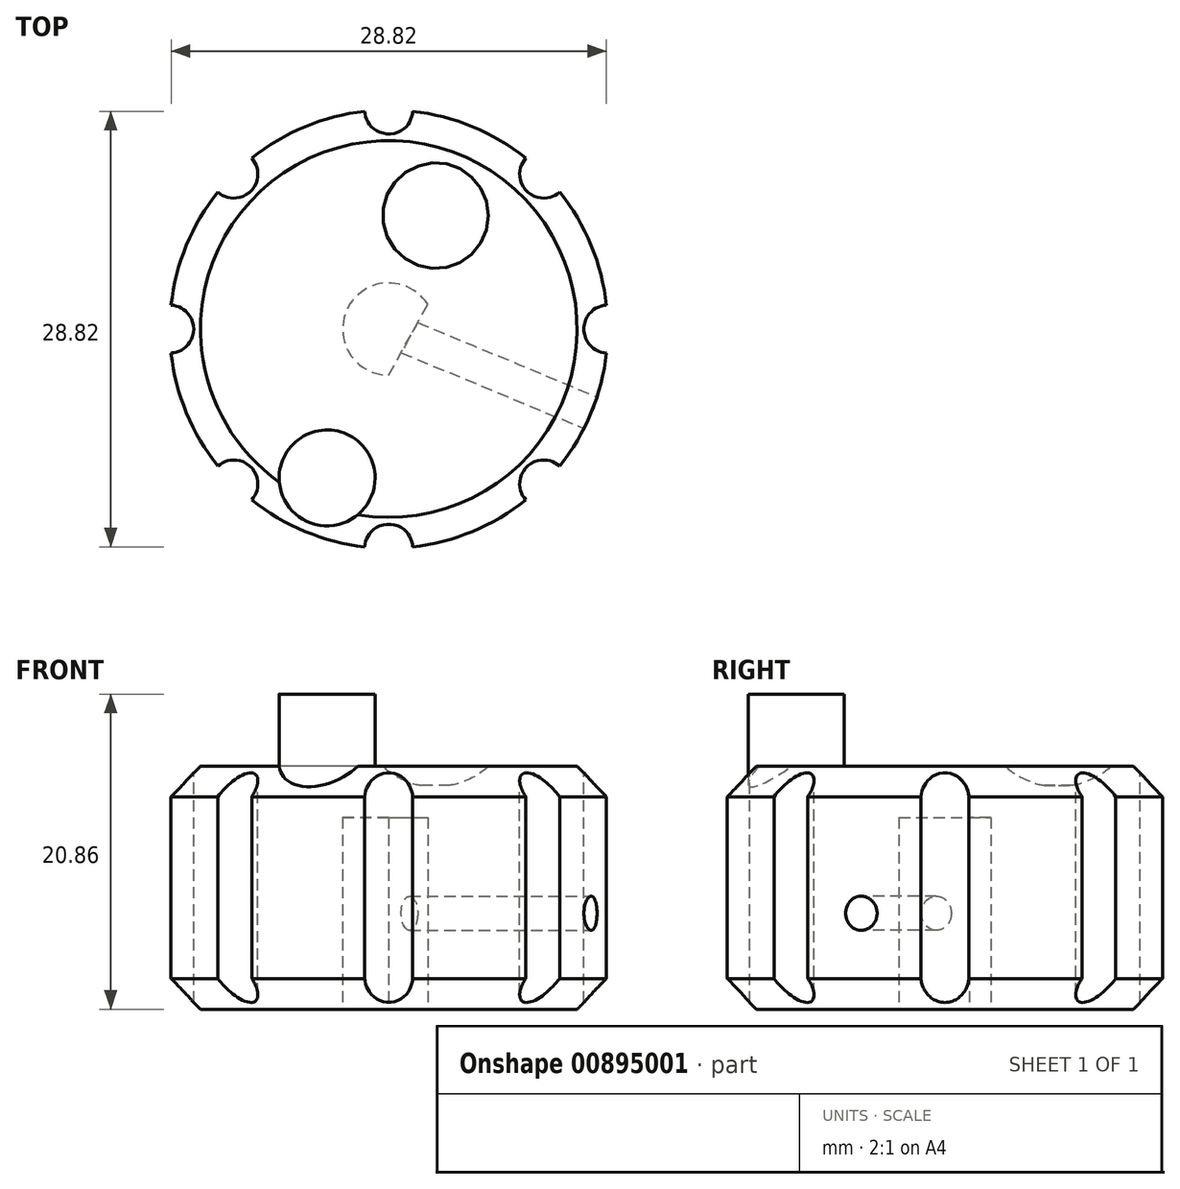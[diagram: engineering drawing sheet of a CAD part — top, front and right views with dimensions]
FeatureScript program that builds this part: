
annotation { "Feature Type Name" : "Feature", "Feature Type Description" : "" }
export const myFeature = defineFeature(function(context is Context, id is Id, definition is map)
    precondition{}
    {
        {
            var Q0;
            Q0=qCreatedBy(makeId("Top.planeOp"),FACE);
            var sketch = newSketch(context, id + "F0", { "sketchPlane" : qUnion([Q0])});
            skCircle(sketch, "E0", {"center": v(0, 0) * mm, "radius": 14.5 * mm});
            skSolve(sketch);
        }
        {
            var Q0;
            Q0 = qSketchRegion(id + "F0", true);
            extrude(context, id + "F1", {"entities" : qUnion([Q0]), "depth" : 16.1 * mm, "offsetDistance" : 25.4 * mm});
        }
        {
            var Q0;
            Q0=makeQuery(id+"F1.opExtrude","CAP_EDGE",EDGE,{"disambiguationData":[OSD([sQuery(id+"F0.wireOp",EDGE,"E0")])],"isStart":false});
            var Q1;
            Q1=makeQuery(id+"F1.opExtrude","CAP_EDGE",EDGE,{"disambiguationData":[OSD([sQuery(id+"F0.wireOp",EDGE,"E0")])],"isStart":true});
            chamfer(context, id + "F2", {"entities" : qUnion([Q0, Q1]), "width" : 2.03 * mm, "tangentPropagation" : true});
        }
        {
            var Q0;
            Q0=makeQuery(id+"F1.opExtrude","CAP_FACE",FACE,{"disambiguationData":[OSD([sQuery(id+"F0.wireOp",EDGE,"E0")])],"isStart":true});
            var sketch = newSketch(context, id + "F3", { "sketchPlane" : qUnion([Q0])});
            skCircle(sketch, "E1", {"center": v(0, 0) * mm, "radius": 3.05 * mm});
            skLineSegment(sketch, "E2", {"start": v(0, 3.05) * mm, "end": v(2.58, -1.63) * mm});
            skLineSegment(sketch, "E3", {"start": v(1.29, 0.7) * mm, "end": v(-2.67, -1.47) * mm, "construction": true});
            skSolve(sketch);
        }
        {
            var Q0;
            {var subQ0=sQuery(id+"F3.wireOp",EDGE,"E2");Q0=makeQuery(id+"F3.imprint","IMPRINT",FACE,{"disambiguationData":[TD([[makeQuery(id+"F3.imprint","IMPRINT",EDGE,{"derivedFrom":subQ0}),-1.0]])]});}
            extrude(context, id + "F4", {"entities" : qUnion([Q0]), "operationType" : NewBodyOperationType.REMOVE, "oppositeDirection" : true, "depth" : 12.7 * mm, "offsetDistance" : 25.4 * mm});
        }
        {
            var Q0;
            Q0=makeQuery(id+"F1.opExtrude","CAP_FACE",FACE,{"disambiguationData":[OSD([sQuery(id+"F0.wireOp",EDGE,"E0")])],"isStart":false});
            var sketch = newSketch(context, id + "F5", { "sketchPlane" : qUnion([Q0])});
            skCircle(sketch, "E4", {"center": v(3.11, 7.5) * mm, "radius": 3.5 * mm});
            skLineSegment(sketch, "E5", {"start": v(0, 0) * mm, "end": v(3.11, 7.5) * mm});
            skSolve(sketch);
        }
        {
            var Q0;
            Q0 = qSketchRegion(id + "F5", true);
            extrude(context, id + "F6", {"entities" : qUnion([Q0]), "operationType" : NewBodyOperationType.REMOVE, "oppositeDirection" : true, "depth" : 1.27 * mm, "offsetDistance" : 25.4 * mm});
        }
        {
            var Q0;
            Q0=makeQuery(id+"F6.boolean.opBoolean","COPY",EDGE,{"derivedFrom":makeQuery(id+"F6.opExtrude","CAP_EDGE",EDGE,{"disambiguationData":[OSD([sQuery(id+"F5.wireOp",EDGE,"E4")])],"isStart":false})});
            fillet(context, id + "F7", {"entities" : qUnion([Q0]), "radius" : 3.17 * mm, "tangentPropagation" : true, "rho" : .3, "crossSection" : FilletCrossSection.CONIC, "allowEdgeOverflow" : false});
        }
        {
            var Q0;
            Q0=makeQuery(id+"F1.opExtrude","CAP_FACE",FACE,{"disambiguationData":[OSD([sQuery(id+"F0.wireOp",EDGE,"E0")])],"isStart":false});
            var sketch = newSketch(context, id + "F8", { "sketchPlane" : qUnion([Q0])});
            skCircle(sketch, "E6.0", {"center": v(0, 0) * mm, "radius": 14.5 * mm});
            skCircle(sketch, "E7", {"center": v(0, 14.5) * mm, "radius": 1.59 * mm});
            skCircle(sketch, "E8.1.0", {"center": v(-10.25, 10.25) * mm, "radius": 1.59 * mm});
            skCircle(sketch, "E8.2.0", {"center": v(-14.5, 0) * mm, "radius": 1.59 * mm});
            skCircle(sketch, "E8.3.0", {"center": v(-10.25, -10.25) * mm, "radius": 1.59 * mm});
            skCircle(sketch, "E8.4.0", {"center": v(0, -14.5) * mm, "radius": 1.59 * mm});
            skCircle(sketch, "E8.5.0", {"center": v(10.25, -10.25) * mm, "radius": 1.59 * mm});
            skCircle(sketch, "E8.6.0", {"center": v(14.5, 0) * mm, "radius": 1.59 * mm});
            skCircle(sketch, "E8.7.0", {"center": v(10.25, 10.25) * mm, "radius": 1.59 * mm});
            skSolve(sketch);
        }
        {
            var Q0;
            {var subQ0=sQuery(id+"F8.wireOp",EDGE,"E7");var subQ1=sQuery(id+"F8.wireOp",EDGE,"E6.0");var subQ2=makeQuery(id+"F8.imprint","INTERSECT",VERTEX,{"disambiguationData":[OD(0.0)],"derivedFrom":[subQ1,subQ0]});Q0=makeQuery(id+"F8.imprint","IMPRINT",FACE,{"disambiguationData":[TD([[makeQuery(id+"F8.imprint","IMPRINT",EDGE,{"disambiguationData":[TD([[subQ2,-1.0]])],"derivedFrom":subQ1}),1.0]])]});}
            var Q1;
            {var subQ0=sQuery(id+"F8.wireOp",EDGE,"E8.7.0");var subQ1=sQuery(id+"F8.wireOp",EDGE,"E6.0");var subQ2=makeQuery(id+"F8.imprint","INTERSECT",VERTEX,{"disambiguationData":[OD(0.0)],"derivedFrom":[subQ1,subQ0]});Q1=makeQuery(id+"F8.imprint","IMPRINT",FACE,{"disambiguationData":[TD([[makeQuery(id+"F8.imprint","IMPRINT",EDGE,{"disambiguationData":[TD([[subQ2,-1.0]])],"derivedFrom":subQ1}),1.0]])]});}
            var Q2;
            {var subQ0=sQuery(id+"F8.wireOp",EDGE,"E8.6.0");var subQ1=sQuery(id+"F8.wireOp",EDGE,"E6.0");var subQ2=makeQuery(id+"F8.imprint","INTERSECT",VERTEX,{"disambiguationData":[OD(0.0)],"derivedFrom":[subQ1,subQ0]});Q2=makeQuery(id+"F8.imprint","IMPRINT",FACE,{"disambiguationData":[TD([[makeQuery(id+"F8.imprint","IMPRINT",EDGE,{"disambiguationData":[TD([[subQ2,1.0]])],"derivedFrom":subQ1}),1.0]])]});}
            var Q3;
            {var subQ0=sQuery(id+"F8.wireOp",EDGE,"E8.5.0");var subQ1=sQuery(id+"F8.wireOp",EDGE,"E6.0");var subQ2=makeQuery(id+"F8.imprint","INTERSECT",VERTEX,{"disambiguationData":[OD(0.0)],"derivedFrom":[subQ1,subQ0]});Q3=makeQuery(id+"F8.imprint","IMPRINT",FACE,{"disambiguationData":[TD([[makeQuery(id+"F8.imprint","IMPRINT",EDGE,{"disambiguationData":[TD([[subQ2,-1.0]])],"derivedFrom":subQ1}),1.0]])]});}
            var Q4;
            {var subQ0=sQuery(id+"F8.wireOp",EDGE,"E8.4.0");var subQ1=sQuery(id+"F8.wireOp",EDGE,"E6.0");var subQ2=makeQuery(id+"F8.imprint","INTERSECT",VERTEX,{"disambiguationData":[OD(0.0)],"derivedFrom":[subQ1,subQ0]});Q4=makeQuery(id+"F8.imprint","IMPRINT",FACE,{"disambiguationData":[TD([[makeQuery(id+"F8.imprint","IMPRINT",EDGE,{"disambiguationData":[TD([[subQ2,-1.0]])],"derivedFrom":subQ1}),1.0]])]});}
            var Q5;
            {var subQ0=sQuery(id+"F8.wireOp",EDGE,"E8.3.0");var subQ1=sQuery(id+"F8.wireOp",EDGE,"E6.0");var subQ2=makeQuery(id+"F8.imprint","INTERSECT",VERTEX,{"disambiguationData":[OD(0.0)],"derivedFrom":[subQ1,subQ0]});Q5=makeQuery(id+"F8.imprint","IMPRINT",FACE,{"disambiguationData":[TD([[makeQuery(id+"F8.imprint","IMPRINT",EDGE,{"disambiguationData":[TD([[subQ2,-1.0]])],"derivedFrom":subQ1}),1.0]])]});}
            var Q6;
            {var subQ0=sQuery(id+"F8.wireOp",EDGE,"E8.2.0");var subQ1=sQuery(id+"F8.wireOp",EDGE,"E6.0");var subQ2=makeQuery(id+"F8.imprint","INTERSECT",VERTEX,{"disambiguationData":[OD(0.0)],"derivedFrom":[subQ1,subQ0]});Q6=makeQuery(id+"F8.imprint","IMPRINT",FACE,{"disambiguationData":[TD([[makeQuery(id+"F8.imprint","IMPRINT",EDGE,{"disambiguationData":[TD([[subQ2,-1.0]])],"derivedFrom":subQ1}),1.0]])]});}
            var Q7;
            {var subQ0=sQuery(id+"F8.wireOp",EDGE,"E8.1.0");var subQ1=sQuery(id+"F8.wireOp",EDGE,"E6.0");var subQ2=makeQuery(id+"F8.imprint","INTERSECT",VERTEX,{"disambiguationData":[OD(0.0)],"derivedFrom":[subQ1,subQ0]});Q7=makeQuery(id+"F8.imprint","IMPRINT",FACE,{"disambiguationData":[TD([[makeQuery(id+"F8.imprint","IMPRINT",EDGE,{"disambiguationData":[TD([[subQ2,-1.0]])],"derivedFrom":subQ1}),1.0]])]});}
            extrude(context, id + "F9", {"entities" : qUnion([Q0, Q1, Q2, Q3, Q4, Q5, Q6, Q7]), "operationType" : NewBodyOperationType.REMOVE, "endBound" : BoundingType.THROUGH_ALL, "oppositeDirection" : true, "depth" : 25.4 * mm, "offsetDistance" : 25.4 * mm});
        }
        {
            var Q0;
            Q0=makeQuery(id+"F1.opExtrude","CAP_FACE",FACE,{"disambiguationData":[OSD([sQuery(id+"F0.wireOp",EDGE,"E0")])],"isStart":false});
            var sketch = newSketch(context, id + "F10", { "sketchPlane" : qUnion([Q0])});
            skCircle(sketch, "E9", {"center": v(-4.08, -9.86) * mm, "radius": 3.18 * mm});
            skLineSegment(sketch, "E10", {"start": v(0, 0) * mm, "end": v(-4.08, -9.86) * mm, "construction": true});
            skSolve(sketch);
        }
        {
            var Q0;
            Q0=makeQuery(id+"F10.imprint","IMPRINT",FACE,{"disambiguationData":[TD([[makeQuery(id+"F10.imprint","IMPRINT",EDGE,{"derivedFrom":sQuery(id+"F10.wireOp",EDGE,"E9")}),1.0]])]});
            extrude(context, id + "F11", {"entities" : qUnion([Q0]), "operationType" : NewBodyOperationType.ADD, "depth" : 4.76 * mm, "offsetDistance" : 25.4 * mm, "hasSecondDirection" : true, "secondDirectionOppositeDirection" : true, "secondDirectionDepth" : 12.7 * mm});
        }
        {
            var Q0;
            {var subQ0=sQuery(id+"F0.wireOp",EDGE,"E0");Q0=makeQuery(id+"F9.boolean.opBoolean","INTERSECT",VERTEX,{"disambiguationData":[OD(1.0)],"derivedFrom":[makeQuery(id+"F2.opChamfer","BLEND_FACE",FACE,{"disambiguationData":[OSD([subQ0]),TDD([makeQuery(id+"F1.opExtrude","CAP_EDGE",EDGE,{"disambiguationData":[OSD([subQ0])],"isStart":false})])]}),makeQuery(id+"F9.opExtrude","SWEPT_FACE",FACE,{"disambiguationData":[OSD([sQuery(id+"F8.wireOp",EDGE,"E8.5.0")])]})]});}
            var Q1;
            {var subQ0=sQuery(id+"F0.wireOp",EDGE,"E0");Q1=makeQuery(id+"F9.boolean.opBoolean","INTERSECT",VERTEX,{"disambiguationData":[OD(1.0)],"derivedFrom":[makeQuery(id+"F2.opChamfer","BLEND_FACE",FACE,{"disambiguationData":[OSD([subQ0]),TDD([makeQuery(id+"F1.opExtrude","CAP_EDGE",EDGE,{"disambiguationData":[OSD([subQ0])],"isStart":false})])]}),makeQuery(id+"F9.opExtrude","SWEPT_FACE",FACE,{"disambiguationData":[OSD([sQuery(id+"F8.wireOp",EDGE,"E8.6.0")])]})]});}
            var Q2;
            {var subQ0=sQuery(id+"F0.wireOp",EDGE,"E0");Q2=makeQuery(id+"F9.boolean.opBoolean","INTERSECT",VERTEX,{"disambiguationData":[OD(1.0)],"derivedFrom":[makeQuery(id+"F2.opChamfer","BLEND_FACE",FACE,{"disambiguationData":[OSD([subQ0]),TDD([makeQuery(id+"F1.opExtrude","CAP_EDGE",EDGE,{"disambiguationData":[OSD([subQ0])],"isStart":true})])]}),makeQuery(id+"F9.opExtrude","SWEPT_FACE",FACE,{"disambiguationData":[OSD([sQuery(id+"F8.wireOp",EDGE,"E8.6.0")])]})]});}
            cPlane(context, id + "F12", {"entities" : qUnion([Q0, Q1, Q2]), "cplaneType" : CPlaneType.THREE_POINT, "offset" : 25.4 * mm, "width" : 152.4 * mm, "height" : 152.4 * mm});
        }
        {
            var Q0;
            Q0=qCreatedBy(id+"F12.planeOp",FACE);
            var sketch = newSketch(context, id + "F13", { "sketchPlane" : qUnion([Q0])});
            skLineSegment(sketch, "E11.0", {"start": v(4.05, 14.07) * mm, "end": v(-4.05, 14.07) * mm, "construction": true});
            skLineSegment(sketch, "E12.0", {"start": v(-4.05, 2.03) * mm, "end": v(4.05, 2.03) * mm, "construction": true});
            skLineSegment(sketch, "E13", {"start": v(0, 14.07) * mm, "end": v(0, 2.03) * mm, "construction": true});
            skCircle(sketch, "E14", {"center": v(0, 6.35) * mm, "radius": 1.13 * mm});
            skSolve(sketch);
        }
        {
            var Q0;
            Q0 = qSketchRegion(id + "F13", true);
            extrude(context, id + "F14", {"entities" : qUnion([Q0]), "operationType" : NewBodyOperationType.REMOVE, "endBound" : BoundingType.UP_TO_NEXT, "oppositeDirection" : true, "depth" : 25.4 * mm, "offsetDistance" : 25.4 * mm, "hasSecondDirection" : true, "secondDirectionBound" : SecondDirectionBoundingType.UP_TO_NEXT, "secondDirectionOppositeDirection" : false, "secondDirectionDepth" : 25.4 * mm});
        }
    });
